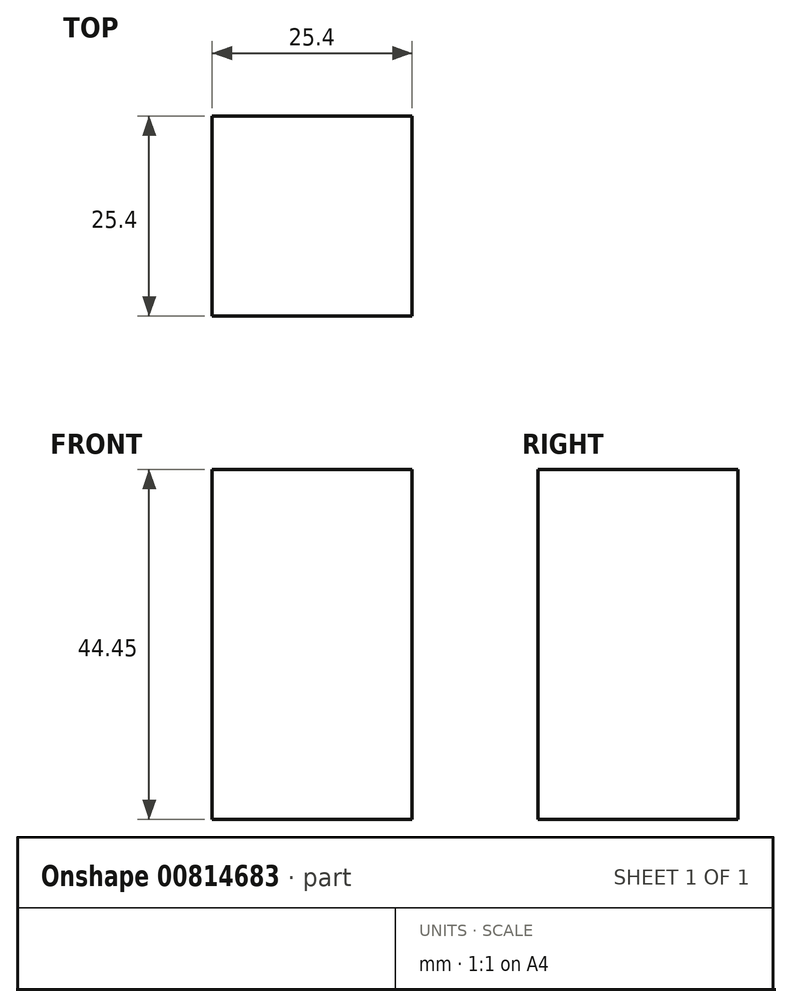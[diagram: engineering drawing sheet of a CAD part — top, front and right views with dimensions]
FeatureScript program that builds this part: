
annotation { "Feature Type Name" : "Feature", "Feature Type Description" : "" }
export const myFeature = defineFeature(function(context is Context, id is Id, definition is map)
    precondition{}
    {
        {
            var Q0;
            Q0=qCreatedBy(makeId("Right.planeOp"),FACE);
            var sketch = newSketch(context, id + "F0", { "sketchPlane" : qUnion([Q0])});
            skLineSegment(sketch, "E0", {"start": v(0, 0) * mm, "end": v(0, 12.7) * mm});
            skLineSegment(sketch, "E1", {"start": v(0, 12.7) * mm, "end": v(0, 44.45) * mm});
            skLineSegment(sketch, "E2", {"start": v(0, 44.45) * mm, "end": v(25.4, 44.45) * mm});
            skLineSegment(sketch, "E3", {"start": v(25.4, 44.45) * mm, "end": v(25.4, -2.95) * mm});
            skLineSegment(sketch, "E4", {"start": v(25.4, 0) * mm, "end": v(-2.64, 0) * mm});
            skSolve(sketch);
        }
        {
            var Q0;
            Q0 = qSketchRegion(id + "F0", true);
            extrude(context, id + "F1", {"entities" : qUnion([Q0]), "depth" : 25.4 * mm, "offsetDistance" : 25.4 * mm});
        }
    });
